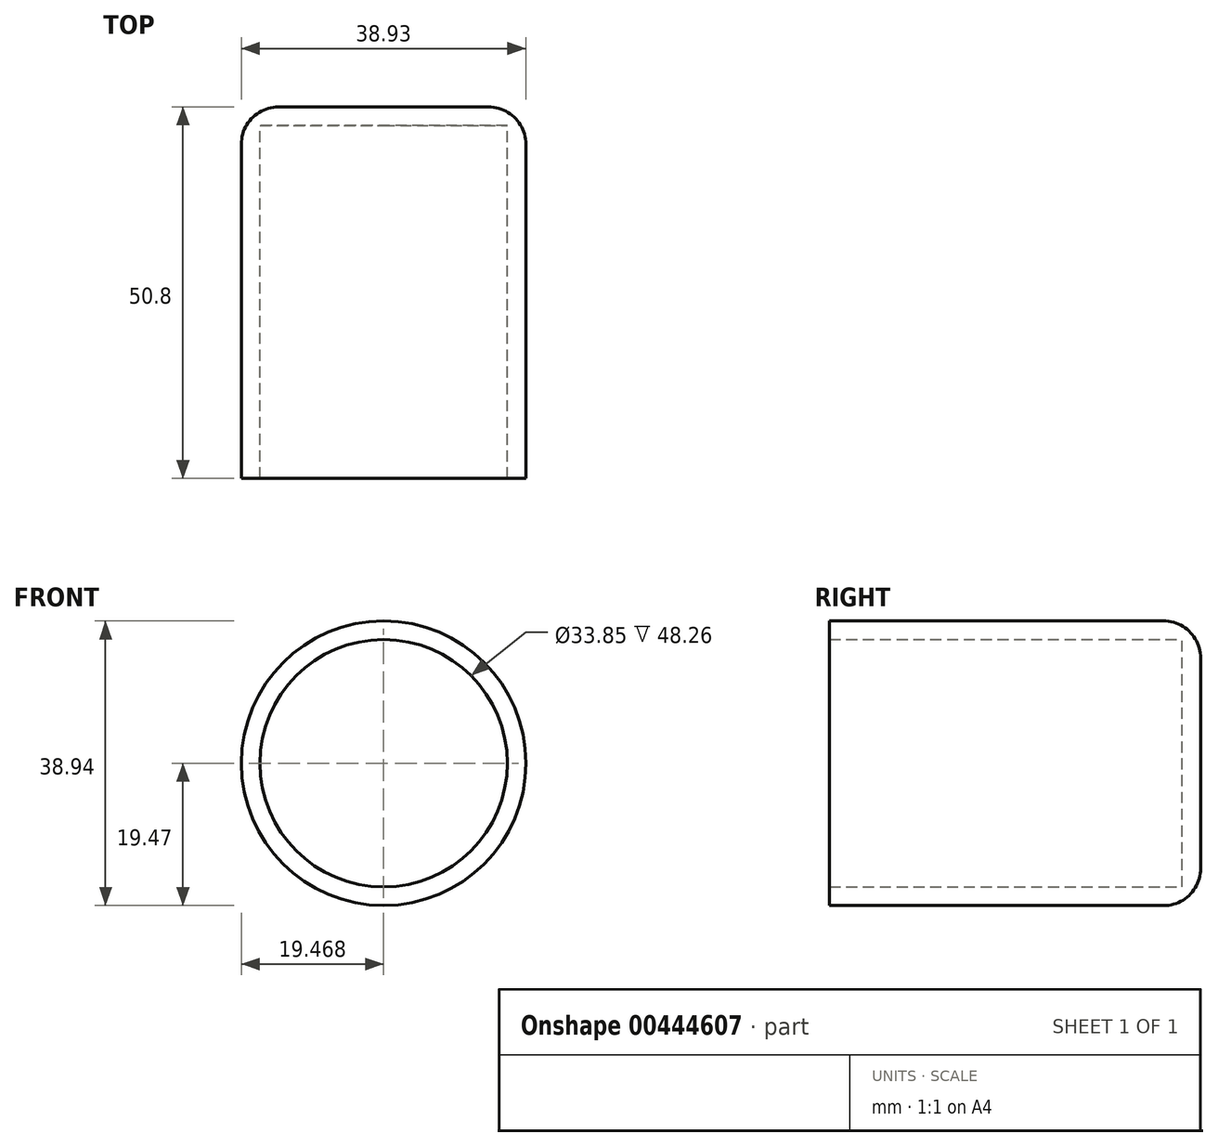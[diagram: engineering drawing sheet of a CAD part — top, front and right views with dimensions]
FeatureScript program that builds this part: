
annotation { "Feature Type Name" : "Feature", "Feature Type Description" : "" }
export const myFeature = defineFeature(function(context is Context, id is Id, definition is map)
    precondition{}
    {
        {
            var Q0;
            Q0=qCreatedBy(makeId("Front.planeOp"),FACE);
            var sketch = newSketch(context, id + "F0", { "sketchPlane" : qUnion([Q0])});
            skCircle(sketch, "E0", {"center": v(-37.8, 38.65) * mm, "radius": 19.47 * mm});
            skSolve(sketch);
        }
        {
            var Q0;
            Q0=makeQuery(id+"F0.imprint","IMPRINT",FACE,{"disambiguationData":[TD([[makeQuery(id+"F0.imprint","IMPRINT",EDGE,{"derivedFrom":sQuery(id+"F0.wireOp",EDGE,"E0")}),1.0]])]});
            extrude(context, id + "F1", {"entities" : qUnion([Q0]), "depth" : 25.4 * mm});
        }
        {
            var Q0;
            Q0=makeQuery(id+"F1.opExtrude","CAP_FACE",FACE,{"disambiguationData":[OSD([sQuery(id+"F0.wireOp",EDGE,"E0")])],"isStart":false});
            shell(context, id + "F2", {"entities" : qUnion([Q0]), "thickness" : 2.54 * mm});
        }
        {
            var Q0;
            Q0=makeQuery(id+"F1.opExtrude","CAP_FACE",FACE,{"disambiguationData":[OSD([sQuery(id+"F0.wireOp",EDGE,"E0")])],"isStart":false});
            extrude(context, id + "F3", {"entities" : qUnion([Q0]), "operationType" : NewBodyOperationType.ADD, "oppositeDirection" : true, "depth" : 25.4 * mm});
        }
        {
            var Q0;
            Q0=makeQuery(id+"F1.opExtrude","CAP_FACE",FACE,{"disambiguationData":[OSD([sQuery(id+"F0.wireOp",EDGE,"E0")])],"isStart":false});
            extrude(context, id + "F4", {"entities" : qUnion([Q0]), "operationType" : NewBodyOperationType.ADD, "depth" : 25.4 * mm});
        }
        {
            var Q0;
            Q0=makeQuery(id+"F1.opExtrude","CAP_FACE",FACE,{"disambiguationData":[OSD([sQuery(id+"F0.wireOp",EDGE,"E0")])],"isStart":true});
            fillet(context, id + "F5", {"entities" : qUnion([Q0]), "radius" : 5.08 * mm, "tangentPropagation" : true, "allowEdgeOverflow" : false});
        }
    });
